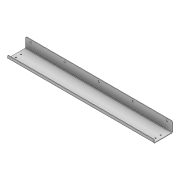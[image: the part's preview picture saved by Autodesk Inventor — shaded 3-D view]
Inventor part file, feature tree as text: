
AUTODESK INVENTOR PART (.ipt)
format: ipt  version: 2020 (Build 240168000, 168)  size: 164,352 bytes
history: native  units: mm
features: sheet_metal_op x7, sketch x6, other x4, hole x3, projected_geometry x3, fillet x1
ambient origin geometry x8: Origin, YZ Plane, XZ Plane, XY Plane, X Axis, Y Axis, Z Axis, Center Point
bodies: Solid1 (feature_tree)
feature tree (24):
  sheet_metal_op  "Face1"
  sheet_metal_op  "Flange1"
  sheet_metal_op  "Flange2"
  hole  "穴1"  [1 undecoded]
  fillet  "フィレット1"  Radius=1.5mm
  hole  "穴2"  [1 undecoded]
  other  "作業平面1"
  hole  "Hole3"  [1 undecoded]
  sketch  "Sketch1"  dims[d0=430.0mm d1=30.0mm d2=1.5mm]
  other  "Plate1"
  sketch  "Sketch2"  dims[d3=1.5mm d4=0.75mm]
  other  "Plate2"
  sheet_metal_op  "Bend1"
  sheet_metal_op  "Corner1"
  sketch  "Sketch3"  dims[d5=3.0mm d6=1.5mm]
  other  "Plate3"
  sheet_metal_op  "Bend2"
  sheet_metal_op  "Corner2"
  sketch  "スケッチ4"
  projected_geometry  "投影ループ1"
  sketch  "スケッチ5"
  projected_geometry  "投影ループ2"
  sketch  "Sketch7"  dims[d7=55.0mm d8=90.0deg d9=1.5mm d10=6.0mm d11=1.5mm d12=1.5mm d13=1.5mm d14=0.75mm d15=3.0mm d16=1.5mm d17=10.0mm d18=90.0deg d19=1.5mm d20=6.0mm d21=1.5mm d22=1.5mm d24=15.0mm d25=15.0mm d27=100.0mm d28=5.2mm d29=6.0mm d30=6.0mm d31=2.0mm d32=90.0deg d33=1.5mm d34=20.594885mm d35=3.0mm d36=15.0mm d40=10.0mm d41=3.242mm d42=8.0mm d43=6.0mm d44=2.0mm d45=90.0deg d46=11.8mm d47=20.594885mm d48=-335.0mm d50=10.0mm d51=3.242mm d52=8.0mm d53=4.0mm d54=2.0mm d55=90.0deg d56=11.8mm d57=20.594885mm d58=100.0mm d59=200.0mm d60=7.5mm d61=19.5mm]
  projected_geometry  "Projected Loop4"
note: 3 required parameter values undecoded (feature->parameter linkage not recoverable at this tier; creation-order binding heuristic only, values carry confidence <= 0.55)
